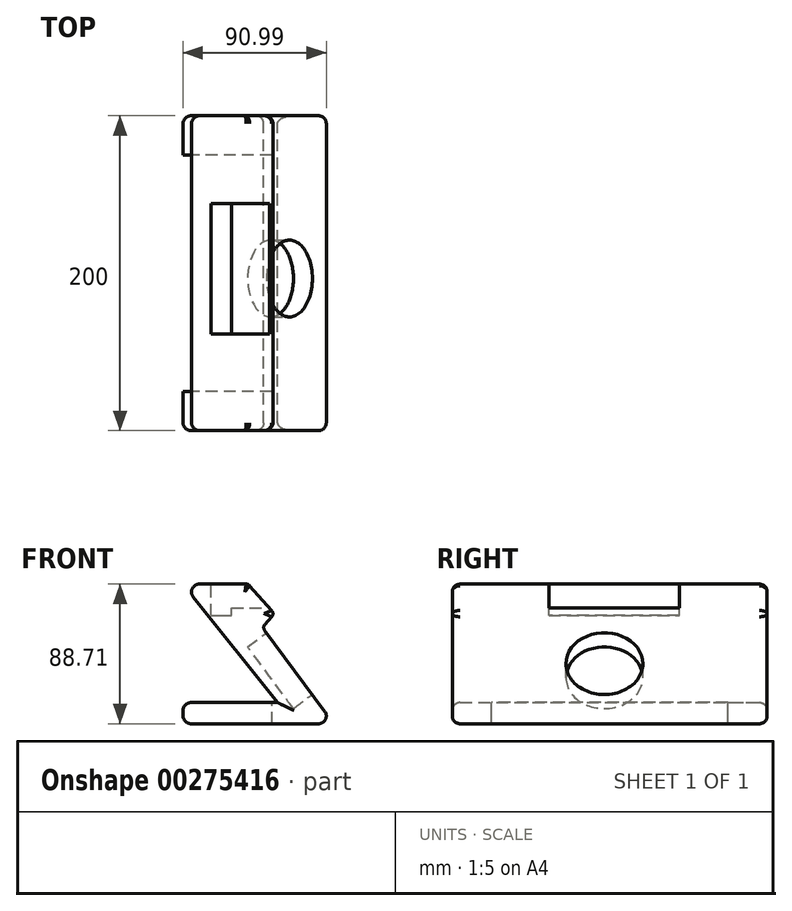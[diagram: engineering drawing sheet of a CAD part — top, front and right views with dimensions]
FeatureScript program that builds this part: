
annotation { "Feature Type Name" : "Feature", "Feature Type Description" : "" }
export const myFeature = defineFeature(function(context is Context, id is Id, definition is map)
    precondition{}
    {
        {
            var Q0;
            Q0=qCreatedBy(makeId("Front.planeOp"),FACE);
            var sketch = newSketch(context, id + "F0", { "sketchPlane" : qUnion([Q0])});
            skLineSegment(sketch, "E0.bottom", {"start": v(-12.37, 45.3) * mm, "end": v(0, 45.3) * mm});
            skLineSegment(sketch, "E0.left", {"start": v(-22.75, -29.92) * mm, "end": v(-22.75, -43.4) * mm});
            skLineSegment(sketch, "E1", {"start": v(-16.27, 37.19) * mm, "end": v(37.25, -29.92) * mm});
            skLineSegment(sketch, "E2", {"start": v(37.25, -29.92) * mm, "end": v(-17.75, -29.92) * mm});
            skLineSegment(sketch, "E3", {"start": v(-22.75, -34.92) * mm, "end": v(-22.75, -38.4) * mm});
            skLineSegment(sketch, "E4", {"start": v(-17.75, -43.4) * mm, "end": v(63.24, -43.4) * mm});
            skPoint(sketch, "E5.end.orphan", {"position": v(0, 45.3) * mm});
            skPoint(sketch, "E6.visualSharp", {"position": v(72.78, -43.4) * mm});
            skArc(sketch, "E6.filletArc", {"start": v(63.24, -43.4) * mm, "mid": v(67.7, -40.65) * mm, "end": v(67.25, -35.42) * mm});
            skPoint(sketch, "E7.visualSharp", {"position": v(-22.75, -43.4) * mm});
            skArc(sketch, "E7.filletArc", {"start": v(-22.75, -38.4) * mm, "mid": v(-21.28, -41.94) * mm, "end": v(-17.75, -43.4) * mm});
            skPoint(sketch, "E8.visualSharp", {"position": v(-22.75, -29.92) * mm});
            skArc(sketch, "E8.filletArc", {"start": v(-17.75, -29.92) * mm, "mid": v(-21.28, -31.38) * mm, "end": v(-22.75, -34.92) * mm});
            skLineSegment(sketch, "E9", {"start": v(67.25, -35.42) * mm, "end": v(29.07, 16.03) * mm});
            skPoint(sketch, "E10.visualSharp", {"position": v(-22.75, 45.3) * mm});
            skArc(sketch, "E10.filletArc", {"start": v(-12.37, 45.3) * mm, "mid": v(-16.87, 42.48) * mm, "end": v(-16.27, 37.19) * mm});
            skLineSegment(sketch, "E11", {"start": v(0, 45.3) * mm, "end": v(17.38, 45.3) * mm});
            skLineSegment(sketch, "E12", {"start": v(19.62, 44.3) * mm, "end": v(33.59, 28.56) * mm});
            skLineSegment(sketch, "E13", {"start": v(33.56, 24.54) * mm, "end": v(29.27, 19.84) * mm});
            skPoint(sketch, "E14.visualSharp", {"position": v(18.73, 45.3) * mm});
            skArc(sketch, "E14.filletArc", {"start": v(19.62, 44.3) * mm, "mid": v(18.6, 45.04) * mm, "end": v(17.38, 45.3) * mm});
            skPoint(sketch, "E15.visualSharp", {"position": v(35.38, 26.54) * mm});
            skArc(sketch, "E15.filletArc", {"start": v(33.56, 24.54) * mm, "mid": v(34.34, 26.54) * mm, "end": v(33.59, 28.56) * mm});
            skPoint(sketch, "E16.visualSharp", {"position": v(27.6, 18.01) * mm});
            skArc(sketch, "E16.filletArc", {"start": v(29.27, 19.84) * mm, "mid": v(28.49, 17.97) * mm, "end": v(29.07, 16.03) * mm});
            skSolve(sketch);
        }
        {
            var Q0;
            Q0=qSketchRegion(id+"F0",true);
            extrude(context, id + "F1", {"entities" : qUnion([Q0]), "depth" : 200 * mm});
        }
        {
            var Q0;
            Q0=makeQuery(id+"F1.opExtrude","SWEPT_FACE",FACE,{"disambiguationData":[OSD([sQuery(id+"F0.wireOp",EDGE,"E0.bottom"),sQuery(id+"F0.wireOp",EDGE,"E11")])]});
            var sketch = newSketch(context, id + "F2", { "sketchPlane" : qUnion([Q0])});
            skLineSegment(sketch, "E17.bottom", {"start": v(-4.98, -138.64) * mm, "end": v(3.02, -138.64) * mm});
            skLineSegment(sketch, "E17.top", {"start": v(-4.98, -55.74) * mm, "end": v(3.02, -55.74) * mm});
            skLineSegment(sketch, "E17.left", {"start": v(-4.98, -138.64) * mm, "end": v(-4.98, -55.74) * mm});
            skLineSegment(sketch, "E17.right", {"start": v(3.02, -138.64) * mm, "end": v(3.02, -55.74) * mm});
            skSolve(sketch);
        }
        {
            var Q0;
            Q0=makeQuery(id+"F2.imprint","IMPRINT",FACE,{"disambiguationData":[TD([[makeQuery(id+"F2.imprint","IMPRINT",EDGE,{"derivedFrom":sQuery(id+"F2.wireOp",EDGE,"E17.bottom")}),1.0]])]});
            extrude(context, id + "F3", {"entities" : qUnion([Q0]), "operationType" : NewBodyOperationType.REMOVE, "oppositeDirection" : true, "depth" : 20 * mm});
        }
        {
            var Q0;
            Q0=makeQuery(id+"F1.opExtrude","SWEPT_FACE",FACE,{"disambiguationData":[OSD([sQuery(id+"F0.wireOp",EDGE,"E9")])]});
            var sketch = newSketch(context, id + "F4", { "sketchPlane" : qUnion([Q0])});
            skCircle(sketch, "E18", {"center": v(-103.38, -30.94) * mm, "radius": 24.4 * mm});
            skSolve(sketch);
        }
        {
            var Q0;
            Q0=makeQuery(id+"F4.imprint","IMPRINT",FACE,{"disambiguationData":[TD([[makeQuery(id+"F4.imprint","IMPRINT",EDGE,{"derivedFrom":sQuery(id+"F4.wireOp",EDGE,"E18")}),1.0]])]});
            extrude(context, id + "F5", {"entities" : qUnion([Q0]), "operationType" : NewBodyOperationType.REMOVE, "oppositeDirection" : true, "depth" : 15 * mm});
        }
        {
            var Q0;
            Q0=makeQuery(id+"F1.opExtrude","CAP_EDGE",EDGE,{"disambiguationData":[OSD([sQuery(id+"F0.wireOp",EDGE,"E9")])],"isStart":false});
            var Q1;
            Q1=makeQuery(id+"F1.opExtrude","CAP_EDGE",EDGE,{"disambiguationData":[OSD([sQuery(id+"F0.wireOp",EDGE,"E9")])],"isStart":true});
            fillet(context, id + "F6", {"entities" : qUnion([Q0, Q1]), "radius" : 5 * mm, "tangentPropagation" : true, "allowEdgeOverflow" : false});
        }
        {
            var Q0;
            Q0=makeQuery(id+"F1.opExtrude","SWEPT_FACE",FACE,{"disambiguationData":[OSD([sQuery(id+"F0.wireOp",EDGE,"E2")])]});
            var sketch = newSketch(context, id + "F7", { "sketchPlane" : qUnion([Q0])});
            skLineSegment(sketch, "E19.bottom", {"start": v(33.64, -25) * mm, "end": v(-35.2, -25) * mm});
            skLineSegment(sketch, "E19.top", {"start": v(33.64, -175) * mm, "end": v(-35.2, -175) * mm});
            skLineSegment(sketch, "E19.left", {"start": v(33.64, -25) * mm, "end": v(33.64, -175) * mm});
            skLineSegment(sketch, "E19.right", {"start": v(-35.2, -25) * mm, "end": v(-35.2, -175) * mm});
            skSolve(sketch);
        }
        {
            var Q0;
            {var subQ0=sQuery(id+"F7.wireOp",EDGE,"E19.left");Q0=makeQuery(id+"F7.imprint","IMPRINT",FACE,{"disambiguationData":[TD([[makeQuery(id+"F7.imprint","IMPRINT",EDGE,{"derivedFrom":subQ0}),-1.0]])]});}
            var Q1;
            Q1=qSketchRegion(id+"F7",true);
            extrude(context, id + "F8", {"entities" : qUnion([Q0, Q1]), "operationType" : NewBodyOperationType.REMOVE, "oppositeDirection" : true, "depth" : 25 * mm});
        }
        {
            var Q0;
            Q0=makeQuery(id+"F1.opExtrude","SWEPT_FACE",FACE,{"disambiguationData":[OSD([sQuery(id+"F0.wireOp",EDGE,"E0.bottom"),sQuery(id+"F0.wireOp",EDGE,"E11")])]});
            var sketch = newSketch(context, id + "F9", { "sketchPlane" : qUnion([Q0])});
            skLineSegment(sketch, "E20.bottom", {"start": v(3.02, -138.64) * mm, "end": v(35.98, -138.64) * mm});
            skLineSegment(sketch, "E20.top", {"start": v(3.02, -55.74) * mm, "end": v(35.98, -55.74) * mm});
            skLineSegment(sketch, "E20.left", {"start": v(3.02, -138.64) * mm, "end": v(3.02, -55.74) * mm});
            skLineSegment(sketch, "E20.right", {"start": v(35.98, -138.64) * mm, "end": v(35.98, -55.74) * mm});
            skSolve(sketch);
        }
        {
            var Q0;
            Q0 = qSketchRegion(id + "F9", true);
            extrude(context, id + "F10", {"entities" : qUnion([Q0]), "operationType" : NewBodyOperationType.REMOVE, "oppositeDirection" : true, "depth" : 15 * mm});
        }
        {
            var Q0;
            Q0=makeQuery(id+"F10.boolean.opBoolean","COPY",FACE,{"derivedFrom":makeQuery(id+"F10.opExtrude","CAP_FACE",FACE,{"disambiguationData":[OSD([sQuery(id+"F9.wireOp",EDGE,"E20.bottom"),sQuery(id+"F9.wireOp",EDGE,"E20.top"),sQuery(id+"F9.wireOp",EDGE,"E20.left"),sQuery(id+"F9.wireOp",EDGE,"E20.right")])],"isStart":false})});
            var sketch = newSketch(context, id + "F11", { "sketchPlane" : qUnion([Q0])});
            skLineSegment(sketch, "E21.bottom", {"start": v(3.02, -55.74) * mm, "end": v(8.12, -55.74) * mm});
            skLineSegment(sketch, "E21.top", {"start": v(3.02, -138.64) * mm, "end": v(8.12, -138.64) * mm});
            skLineSegment(sketch, "E21.left", {"start": v(3.02, -55.74) * mm, "end": v(3.02, -138.64) * mm});
            skLineSegment(sketch, "E21.right", {"start": v(8.12, -55.74) * mm, "end": v(8.12, -138.64) * mm});
            skSolve(sketch);
        }
        {
            var Q0;
            Q0 = qSketchRegion(id + "F11", true);
            extrude(context, id + "F12", {"entities" : qUnion([Q0]), "operationType" : NewBodyOperationType.REMOVE, "oppositeDirection" : true, "depth" : 5 * mm});
        }
    });
